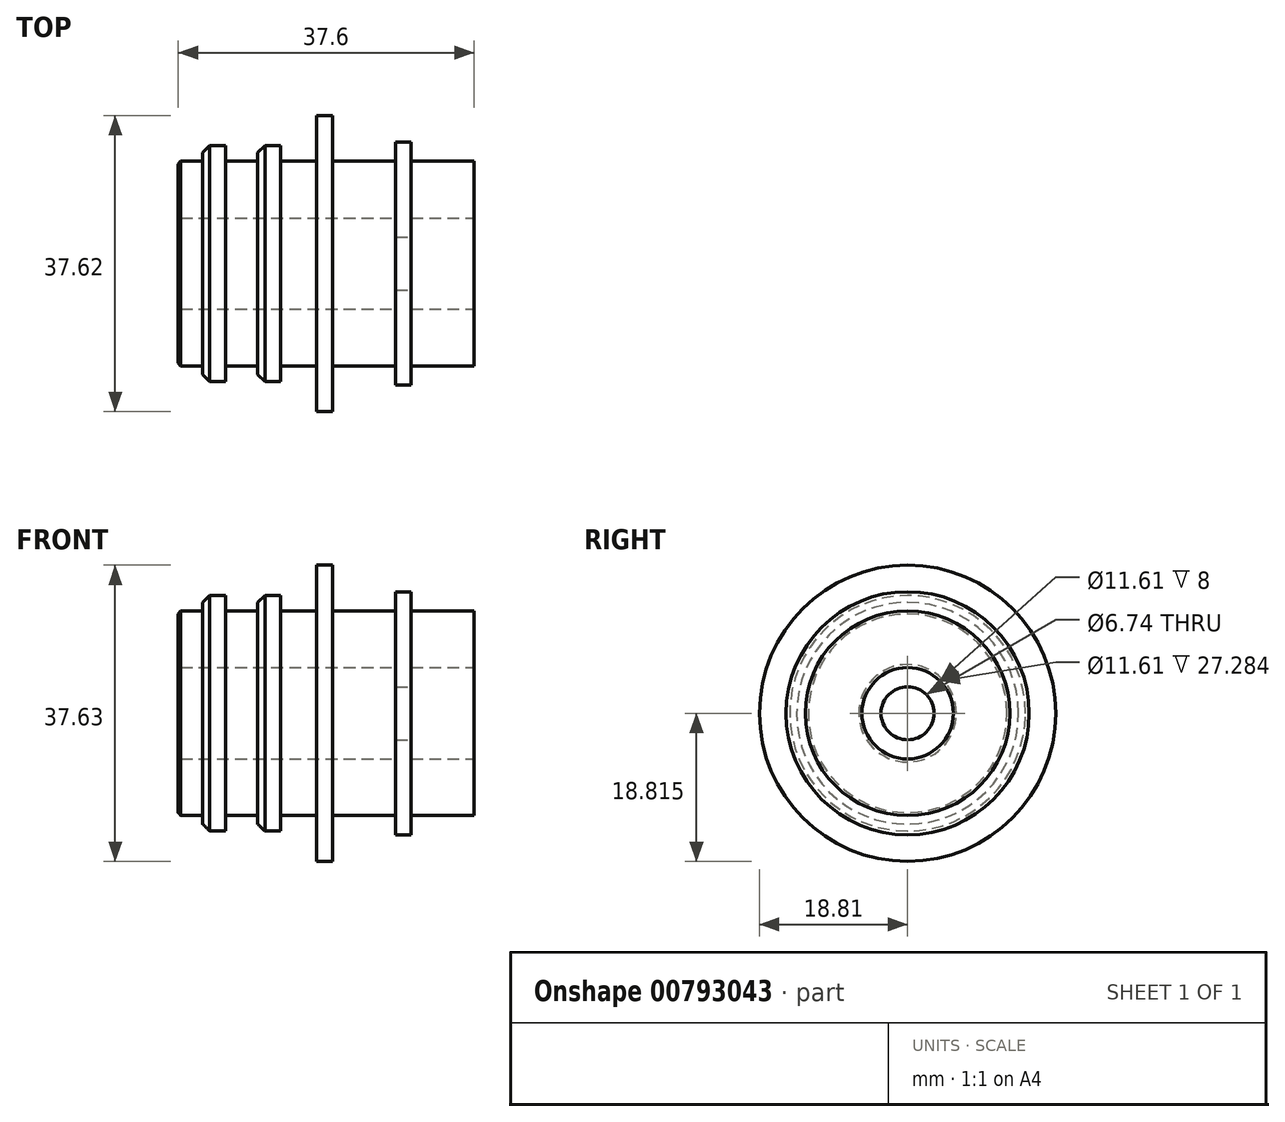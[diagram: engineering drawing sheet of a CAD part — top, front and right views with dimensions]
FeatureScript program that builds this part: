
annotation { "Feature Type Name" : "Feature", "Feature Type Description" : "" }
export const myFeature = defineFeature(function(context is Context, id is Id, definition is map)
    precondition{}
    {
        {
            var Q0;
            Q0=qCreatedBy(makeId("Front.planeOp"),FACE);
            var sketch = newSketch(context, id + "F0", { "sketchPlane" : qUnion([Q0])});
            skLineSegment(sketch, "E0.bottom", {"start": v(18.8, 2.25) * mm, "end": v(-18.8, 2.25) * mm});
            skLineSegment(sketch, "E0.top", {"start": v(18.8, -2.25) * mm, "end": v(-18.8, -2.25) * mm});
            skLineSegment(sketch, "E0.left", {"start": v(18.8, 2.25) * mm, "end": v(18.8, -2.25) * mm});
            skLineSegment(sketch, "E0.right", {"start": v(-18.8, 2.25) * mm, "end": v(-18.8, -2.25) * mm});
            skPoint(sketch, "E0.middle", {"position": v(0, 0) * mm});
            skLineSegment(sketch, "E1", {"start": v(18.8, 2.25) * mm, "end": v(18.8, 3.6) * mm});
            skLineSegment(sketch, "E2", {"start": v(18.8, -2.25) * mm, "end": v(18.8, -3.6) * mm});
            skLineSegment(sketch, "E3", {"start": v(18.8, 3.6) * mm, "end": v(10.8, 3.6) * mm});
            skLineSegment(sketch, "E4", {"start": v(10.8, 3.6) * mm, "end": v(10.8, 6.03) * mm});
            skLineSegment(sketch, "E5", {"start": v(10.8, 6.03) * mm, "end": v(8.8, 6.03) * mm});
            skLineSegment(sketch, "E6", {"start": v(8.8, 6.03) * mm, "end": v(8.8, 3.6) * mm});
            skLineSegment(sketch, "E7", {"start": v(8.8, 3.6) * mm, "end": v(0.8, 3.6) * mm});
            skLineSegment(sketch, "E8", {"start": v(0.8, 3.6) * mm, "end": v(0.8, 9.4) * mm});
            skLineSegment(sketch, "E9", {"start": v(0.8, 9.4) * mm, "end": v(-1.2, 9.4) * mm});
            skLineSegment(sketch, "E10", {"start": v(-1.2, 9.4) * mm, "end": v(-1.2, 3.6) * mm});
            skLineSegment(sketch, "E11", {"start": v(-1.2, 3.6) * mm, "end": v(-5.8, 3.6) * mm});
            skLineSegment(sketch, "E12", {"start": v(-5.8, 3.6) * mm, "end": v(-5.8, 5.56) * mm});
            skLineSegment(sketch, "E13", {"start": v(-5.8, 5.56) * mm, "end": v(-7.8, 5.56) * mm});
            skLineSegment(sketch, "E14", {"start": v(-7.8, 5.56) * mm, "end": v(-8.7, 4.68) * mm});
            skLineSegment(sketch, "E15", {"start": v(-8.7, 4.68) * mm, "end": v(-8.7, 3.6) * mm});
            skLineSegment(sketch, "E16", {"start": v(-8.7, 3.6) * mm, "end": v(-12.8, 3.6) * mm});
            skLineSegment(sketch, "E17", {"start": v(-12.8, 3.6) * mm, "end": v(-12.8, 5.56) * mm});
            skLineSegment(sketch, "E18", {"start": v(-12.8, 5.56) * mm, "end": v(-14.8, 5.56) * mm});
            skLineSegment(sketch, "E19", {"start": v(-14.8, 5.56) * mm, "end": v(-15.7, 4.68) * mm});
            skLineSegment(sketch, "E20", {"start": v(-15.7, 4.68) * mm, "end": v(-15.7, 3.6) * mm});
            skLineSegment(sketch, "E21", {"start": v(-15.7, -3.6) * mm, "end": v(-15.7, -4.68) * mm});
            skLineSegment(sketch, "E22", {"start": v(-15.7, -4.68) * mm, "end": v(-14.8, -5.56) * mm});
            skLineSegment(sketch, "E23", {"start": v(-14.8, -5.56) * mm, "end": v(-12.8, -5.56) * mm});
            skLineSegment(sketch, "E24", {"start": v(-12.8, -5.56) * mm, "end": v(-12.8, -3.6) * mm});
            skLineSegment(sketch, "E25", {"start": v(-12.8, -3.6) * mm, "end": v(-8.7, -3.6) * mm});
            skLineSegment(sketch, "E26", {"start": v(-8.7, -3.6) * mm, "end": v(-8.7, -4.68) * mm});
            skLineSegment(sketch, "E27", {"start": v(-8.7, -4.68) * mm, "end": v(-7.8, -5.56) * mm});
            skLineSegment(sketch, "E28", {"start": v(-7.8, -5.56) * mm, "end": v(-5.8, -5.56) * mm});
            skLineSegment(sketch, "E29", {"start": v(-5.8, -5.56) * mm, "end": v(-5.8, -3.6) * mm});
            skLineSegment(sketch, "E30", {"start": v(-5.8, -3.6) * mm, "end": v(-1.2, -3.6) * mm});
            skLineSegment(sketch, "E31", {"start": v(-1.2, -3.6) * mm, "end": v(-1.2, -9.4) * mm});
            skLineSegment(sketch, "E32", {"start": v(-1.2, -9.4) * mm, "end": v(0.8, -9.4) * mm});
            skLineSegment(sketch, "E33", {"start": v(0.8, -9.4) * mm, "end": v(0.8, -3.6) * mm});
            skLineSegment(sketch, "E34", {"start": v(0.8, -3.6) * mm, "end": v(8.8, -3.6) * mm});
            skLineSegment(sketch, "E35", {"start": v(8.8, -3.6) * mm, "end": v(8.8, -6.03) * mm});
            skLineSegment(sketch, "E36", {"start": v(8.8, -6.03) * mm, "end": v(10.8, -6.03) * mm});
            skLineSegment(sketch, "E37", {"start": v(10.8, -6.03) * mm, "end": v(10.8, -3.6) * mm});
            skLineSegment(sketch, "E38", {"start": v(10.8, -3.6) * mm, "end": v(18.8, -3.6) * mm});
            skLineSegment(sketch, "E39", {"start": v(-15.7, 3.6) * mm, "end": v(-18.48, 3.6) * mm});
            skLineSegment(sketch, "E40", {"start": v(-18.48, 3.6) * mm, "end": v(-18.8, 3.21) * mm});
            skLineSegment(sketch, "E41", {"start": v(-18.8, 3.21) * mm, "end": v(-18.8, 2.25) * mm});
            skLineSegment(sketch, "E42", {"start": v(-15.7, -3.6) * mm, "end": v(-18.48, -3.6) * mm});
            skLineSegment(sketch, "E43", {"start": v(-18.48, -3.6) * mm, "end": v(-18.8, -3.21) * mm});
            skLineSegment(sketch, "E44", {"start": v(-18.8, -3.21) * mm, "end": v(-18.8, -2.25) * mm});
            skLineSegment(sketch, "E45", {"start": v(-18.8, 0) * mm, "end": v(18.8, 0) * mm, "construction": true});
            skSolve(sketch);
        }
        {
            var Q0;
            Q0=makeQuery(id+"F0.imprint","IMPRINT",FACE,{"disambiguationData":[TD([[makeQuery(id+"F0.imprint","IMPRINT",EDGE,{"derivedFrom":sQuery(id+"F0.wireOp",EDGE,"E0.bottom")}),-1.0]])]});
            var Q1;
            Q1=makeQuery(id+"F0.imprint","IMPRINT",FACE,{"disambiguationData":[TD([[makeQuery(id+"F0.imprint","IMPRINT",EDGE,{"derivedFrom":sQuery(id+"F0.wireOp",EDGE,"E0.top")}),1.0]])]});
            var Q2;
            Q2=makeQuery(id+"F0.imprint","IMPRINT",FACE,{"disambiguationData":[TD([[makeQuery(id+"F0.imprint","IMPRINT",EDGE,{"derivedFrom":sQuery(id+"F0.wireOp",EDGE,"E0.bottom")}),1.0]])]});
            var Q3;
            Q3=sQuery(id+"F0.wireOp",EDGE,"E9");
            revolve(context, id + "F1", {"surfaceOperationType" : NewSurfaceOperationType.NEW, "entities" : qUnion([Q0, Q1, Q2]), "axis" : qUnion([Q3]), "revolveType" : RevolveType.FULL});
        }
        {
            var Q0;
            Q0=makeQuery(id+"F1.opRevolve","SWEPT_FACE",FACE,{"disambiguationData":[OSD([sQuery(id+"F0.wireOp",EDGE,"E8")])]});
            extrude(context, id + "F2", {"entities" : qUnion([Q0]), "operationType" : NewBodyOperationType.REMOVE, "oppositeDirection" : true, "depth" : 25.4 * mm, "offsetDistance" : 25.4 * mm});
        }
    });
